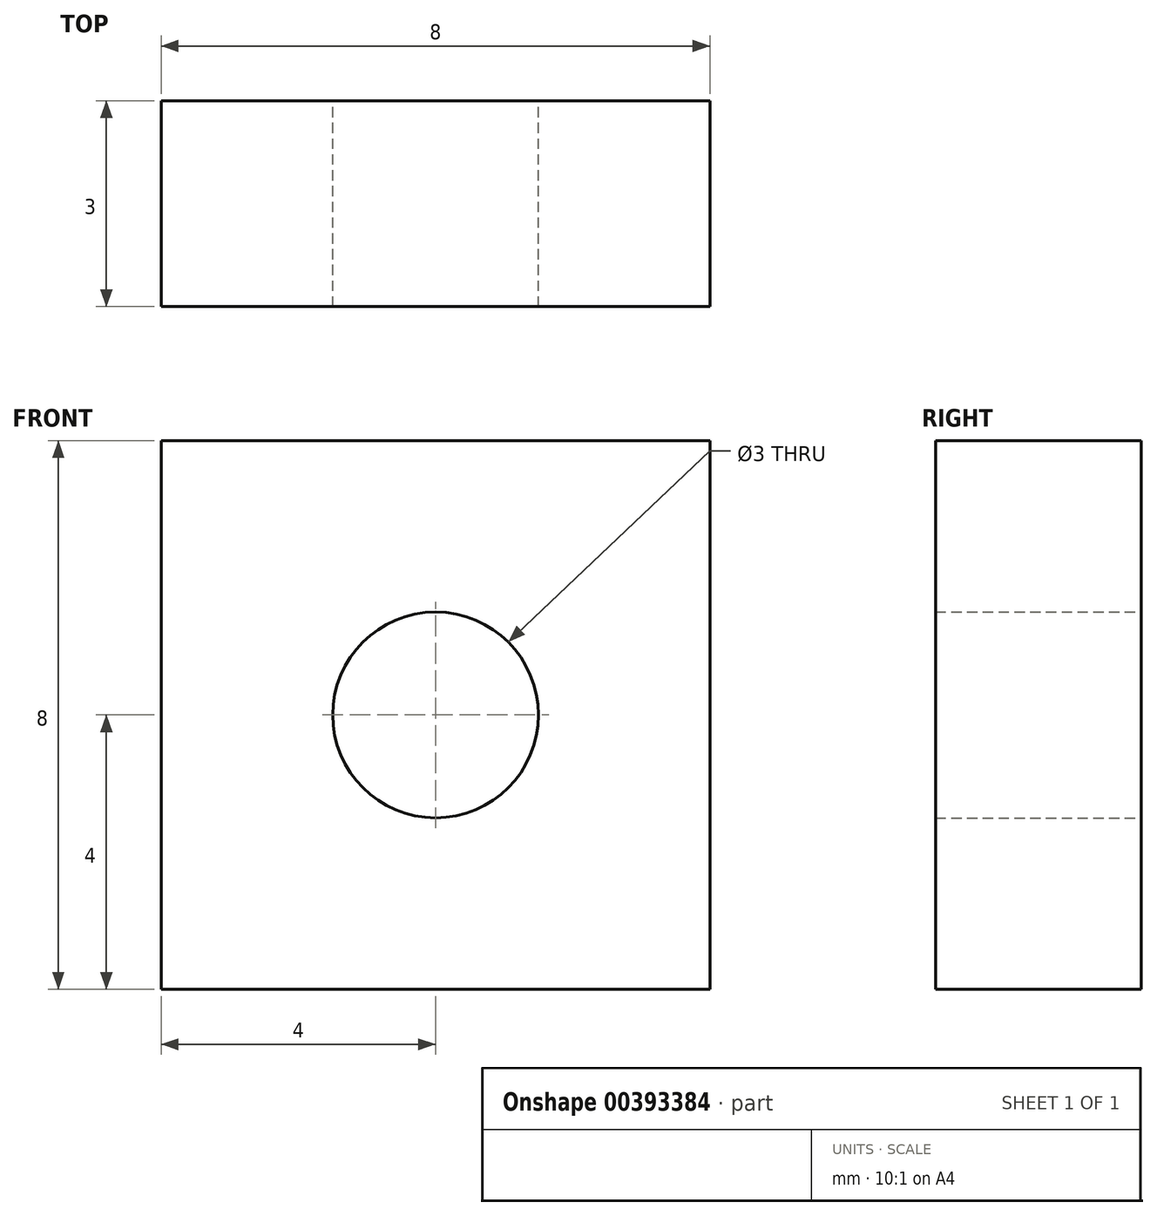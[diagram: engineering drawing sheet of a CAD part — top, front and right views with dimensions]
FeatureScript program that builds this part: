
annotation { "Feature Type Name" : "Feature", "Feature Type Description" : "" }
export const myFeature = defineFeature(function(context is Context, id is Id, definition is map)
    precondition{}
    {
        {
            var Q0;
            Q0=qCreatedBy(makeId("Front.planeOp"),FACE);
            var sketch = newSketch(context, id + "F0", { "sketchPlane" : qUnion([Q0])});
            skCircle(sketch, "E0", {"center": v(0, 0) * mm, "radius": 1.5 * mm});
            skLineSegment(sketch, "E1.bottom", {"start": v(-4, 4) * mm, "end": v(4, 4) * mm});
            skLineSegment(sketch, "E1.top", {"start": v(-4, -4) * mm, "end": v(4, -4) * mm});
            skLineSegment(sketch, "E1.left", {"start": v(-4, 4) * mm, "end": v(-4, -4) * mm});
            skLineSegment(sketch, "E1.right", {"start": v(4, 4) * mm, "end": v(4, -4) * mm});
            skSolve(sketch);
        }
        {
            var Q0;
            Q0=makeQuery(id+"F0.imprint","IMPRINT",FACE,{"disambiguationData":[TD([[makeQuery(id+"F0.imprint","IMPRINT",EDGE,{"derivedFrom":sQuery(id+"F0.wireOp",EDGE,"E0")}),-1.0]])]});
            extrude(context, id + "F1", {"entities" : qUnion([Q0]), "depth" : 3 * mm});
        }
    });
